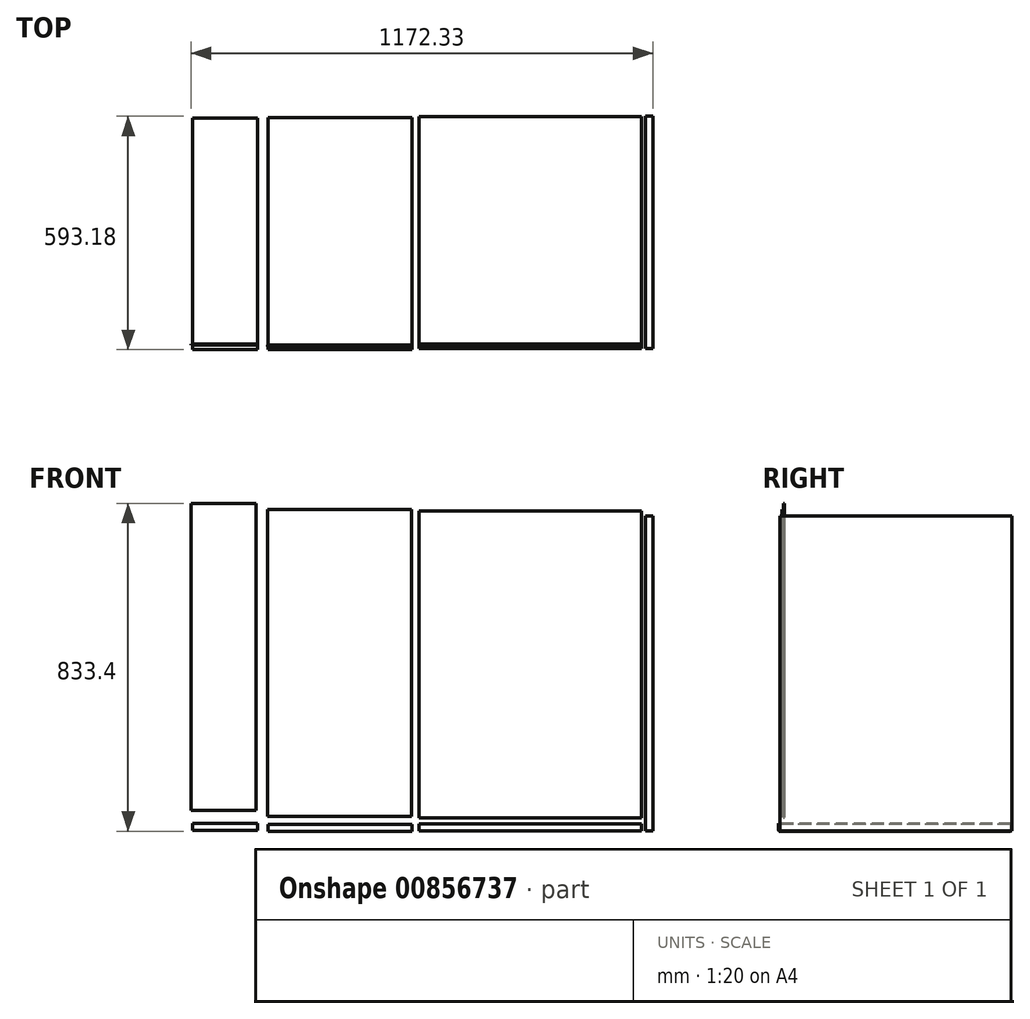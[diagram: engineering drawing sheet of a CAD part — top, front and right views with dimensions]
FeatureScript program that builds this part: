
annotation { "Feature Type Name" : "Feature", "Feature Type Description" : "" }
export const myFeature = defineFeature(function(context is Context, id is Id, definition is map)
    precondition{}
    {
        {
            var Q0;
            Q0=qCreatedBy(makeId("Top.planeOp"),FACE);
            var sketch = newSketch(context, id + "F0", { "sketchPlane" : qUnion([Q0])});
            skLineSegment(sketch, "E0.bottom", {"start": v(109.1, -315.54) * mm, "end": v(127.1, -315.54) * mm});
            skLineSegment(sketch, "E0.top", {"start": v(109.1, 274.46) * mm, "end": v(127.1, 274.46) * mm});
            skLineSegment(sketch, "E0.left", {"start": v(109.1, -315.54) * mm, "end": v(109.1, 274.46) * mm});
            skLineSegment(sketch, "E0.right", {"start": v(127.1, -315.54) * mm, "end": v(127.1, 274.46) * mm});
            skSolve(sketch);
        }
        {
            var Q0;
            Q0 = qSketchRegion(id + "F0", true);
            extrude(context, id + "F1", {"entities" : qUnion([Q0]), "depth" : 800 * mm, "offsetDistance" : 25 * mm});
        }
        {
            var Q0;
            Q0=qCreatedBy(makeId("Front.planeOp"),FACE);
            var sketch = newSketch(context, id + "F2", { "sketchPlane" : qUnion([Q0])});
            skLineSegment(sketch, "E1.bottom", {"start": v(-565, 364.26) * mm, "end": v(0, 364.26) * mm});
            skLineSegment(sketch, "E1.top", {"start": v(-565, -415.74) * mm, "end": v(0, -415.74) * mm});
            skLineSegment(sketch, "E1.left", {"start": v(-565, 364.26) * mm, "end": v(-565, -415.74) * mm});
            skLineSegment(sketch, "E1.right", {"start": v(0, 364.26) * mm, "end": v(0, -415.74) * mm});
            skSolve(sketch);
        }
        {
            var Q0;
            Q0 = qSketchRegion(id + "F2", true);
            extrude(context, id + "F3", {"entities" : qUnion([Q0]), "depth" : 3 * mm, "offsetDistance" : 25 * mm});
        }
        {
            var Q0;
            Q0=qCreatedBy(makeId("Top.planeOp"),FACE);
            var sketch = newSketch(context, id + "F4", { "sketchPlane" : qUnion([Q0])});
            skLineSegment(sketch, "E2.bottom", {"start": v(-523.86, -157.25) * mm, "end": v(41.14, -157.25) * mm});
            skLineSegment(sketch, "E2.top", {"start": v(-523.86, 431.75) * mm, "end": v(41.14, 431.75) * mm});
            skLineSegment(sketch, "E2.left", {"start": v(-523.86, -157.25) * mm, "end": v(-523.86, 431.75) * mm});
            skLineSegment(sketch, "E2.right", {"start": v(41.14, -157.25) * mm, "end": v(41.14, 431.75) * mm});
            skSolve(sketch);
        }
        {
            var Q0;
            Q0=makeQuery(id+"F4.imprint","IMPRINT",FACE,{"disambiguationData":[TD([[makeQuery(id+"F4.imprint","IMPRINT",EDGE,{"derivedFrom":sQuery(id+"F4.wireOp",EDGE,"E2.bottom")}),1.0]])]});
            extrude(context, id + "F5", {"entities" : qUnion([Q0]), "depth" : 18 * mm, "offsetDistance" : 25 * mm});
        }
        {
            var Q0;
            Q0=makeQuery(id+"F5.opExtrude","SWEPT_BODY",BODY,{"disambiguationData":[OSD([sQuery(id+"F4.wireOp",EDGE,"E2.bottom"),sQuery(id+"F4.wireOp",EDGE,"E2.top"),sQuery(id+"F4.wireOp",EDGE,"E2.left"),sQuery(id+"F4.wireOp",EDGE,"E2.right")])]});
            transform(context, id + "F6", {"entities" : qUnion([Q0]), "transformType" : TransformType.TRANSLATION_3D, "dx" : -113 * mm, "dy" : -67 * mm, "dz" : -330 * mm, "makeCopy" : false});
        }
        {
            var Q0;
            Q0=makeQuery(id+"F5.opExtrude","SWEPT_BODY",BODY,{"disambiguationData":[OSD([sQuery(id+"F4.wireOp",EDGE,"E2.bottom"),sQuery(id+"F4.wireOp",EDGE,"E2.top"),sQuery(id+"F4.wireOp",EDGE,"E2.left"),sQuery(id+"F4.wireOp",EDGE,"E2.right")])]});
            transform(context, id + "F7", {"entities" : qUnion([Q0]), "transformType" : TransformType.TRANSLATION_3D, "dx" : -127 * mm, "dy" : 213 * mm, "dz" : -119 * mm, "makeCopy" : false});
        }
        {
            var Q0;
            Q0=makeQuery(id+"F1.opExtrude","SWEPT_BODY",BODY,{"disambiguationData":[OSD([sQuery(id+"F0.wireOp",EDGE,"E0.bottom"),sQuery(id+"F0.wireOp",EDGE,"E0.top"),sQuery(id+"F0.wireOp",EDGE,"E0.left"),sQuery(id+"F0.wireOp",EDGE,"E0.right")])]});
            transform(context, id + "F8", {"entities" : qUnion([Q0]), "transformType" : TransformType.TRANSLATION_3D, "dx" : -98 * mm, "dy" : 304 * mm, "dz" : -449 * mm, "makeCopy" : false});
        }
        {
            var Q0;
            Q0=makeQuery(id+"F5.opExtrude","SWEPT_BODY",BODY,{"disambiguationData":[OSD([sQuery(id+"F4.wireOp",EDGE,"E2.bottom"),sQuery(id+"F4.wireOp",EDGE,"E2.top"),sQuery(id+"F4.wireOp",EDGE,"E2.left"),sQuery(id+"F4.wireOp",EDGE,"E2.right")])]});
            transform(context, id + "F9", {"entities" : qUnion([Q0]), "transformType" : TransformType.TRANSLATION_3D, "dx" : 0 * mm, "dy" : 0 * mm, "dz" : -52 * mm, "makeCopy" : true});
        }
        {
            var Q0;
            Q0=makeQuery(id+"F9.opPattern","COPY",BODY,{"derivedFrom":makeQuery(id+"F5.opExtrude","SWEPT_BODY",BODY,{"disambiguationData":[OSD([sQuery(id+"F4.wireOp",EDGE,"E2.bottom"),sQuery(id+"F4.wireOp",EDGE,"E2.top"),sQuery(id+"F4.wireOp",EDGE,"E2.left"),sQuery(id+"F4.wireOp",EDGE,"E2.right")])]}),"instanceName":"1"});
            deleteBodies(context, id + "F10", {"entities" : qUnion([Q0])});
        }
        {
            var Q0;
            Q0=makeQuery(id+"F4.imprint","IMPRINT",FACE,{"disambiguationData":[TD([[makeQuery(id+"F4.imprint","IMPRINT",EDGE,{"derivedFrom":sQuery(id+"F4.wireOp",EDGE,"E2.bottom")}),1.0]])]});
            var sketch = newSketch(context, id + "F11", { "sketchPlane" : qUnion([Q0])});
            skLineSegment(sketch, "E3.bottom", {"start": v(-1010.8, 367.55) * mm, "end": v(-645.8, 367.55) * mm});
            skLineSegment(sketch, "E3.top", {"start": v(-1010.8, -221.45) * mm, "end": v(-645.8, -221.45) * mm});
            skLineSegment(sketch, "E3.left", {"start": v(-1010.8, 367.55) * mm, "end": v(-1010.8, -221.45) * mm});
            skLineSegment(sketch, "E3.right", {"start": v(-645.8, 367.55) * mm, "end": v(-645.8, -221.45) * mm});
            skSolve(sketch);
        }
        {
            var Q0;
            Q0=makeQuery(id+"F5.opExtrude","SWEPT_BODY",BODY,{"disambiguationData":[OSD([sQuery(id+"F4.wireOp",EDGE,"E2.bottom"),sQuery(id+"F4.wireOp",EDGE,"E2.top"),sQuery(id+"F4.wireOp",EDGE,"E2.left"),sQuery(id+"F4.wireOp",EDGE,"E2.right")])]});
            transform(context, id + "F12", {"entities" : qUnion([Q0]), "transformType" : TransformType.TRANSLATION_3D, "dx" : 199 * mm, "dy" : 0 * mm, "dz" : 0 * mm, "makeCopy" : false});
        }
        {
            var Q0;
            Q0=makeQuery(id+"F11.imprint","IMPRINT",FACE,{"disambiguationData":[TD([[makeQuery(id+"F11.imprint","IMPRINT",EDGE,{"derivedFrom":sQuery(id+"F11.wireOp",EDGE,"E3.bottom")}),-1.0]])]});
            extrude(context, id + "F13", {"entities" : qUnion([Q0]), "depth" : 18 * mm, "offsetDistance" : 25 * mm});
        }
        {
            var Q0;
            Q0=makeQuery(id+"F13.opExtrude","SWEPT_BODY",BODY,{"disambiguationData":[OSD([sQuery(id+"F11.wireOp",EDGE,"E3.bottom"),sQuery(id+"F11.wireOp",EDGE,"E3.top"),sQuery(id+"F11.wireOp",EDGE,"E3.left"),sQuery(id+"F11.wireOp",EDGE,"E3.right")])]});
            transform(context, id + "F14", {"entities" : qUnion([Q0]), "transformType" : TransformType.TRANSLATION_3D, "dx" : 63 * mm, "dy" : 207 * mm, "dz" : -450 * mm, "makeCopy" : false});
        }
        {
            var Q0;
            Q0=makeQuery(id+"F3.opExtrude","CAP_FACE",FACE,{"disambiguationData":[OSD([sQuery(id+"F2.wireOp",EDGE,"E1.bottom"),sQuery(id+"F2.wireOp",EDGE,"E1.top"),sQuery(id+"F2.wireOp",EDGE,"E1.left"),sQuery(id+"F2.wireOp",EDGE,"E1.right")])],"isStart":false});
            var sketch = newSketch(context, id + "F15", { "sketchPlane" : qUnion([Q0])});
            skLineSegment(sketch, "E4.bottom", {"start": v(-1125.1, 719.67) * mm, "end": v(-760.1, 719.67) * mm});
            skLineSegment(sketch, "E4.top", {"start": v(-1125.1, -60.33) * mm, "end": v(-760.1, -60.33) * mm});
            skLineSegment(sketch, "E4.left", {"start": v(-1125.1, 719.67) * mm, "end": v(-1125.1, -60.33) * mm});
            skLineSegment(sketch, "E4.right", {"start": v(-760.1, 719.67) * mm, "end": v(-760.1, -60.33) * mm});
            skSolve(sketch);
        }
        {
            var Q0;
            Q0=makeQuery(id+"F15.imprint","IMPRINT",FACE,{"disambiguationData":[TD([[makeQuery(id+"F15.imprint","IMPRINT",EDGE,{"derivedFrom":sQuery(id+"F15.wireOp",EDGE,"E4.bottom")}),-1.0]])]});
            extrude(context, id + "F16", {"entities" : qUnion([Q0]), "depth" : 3 * mm, "offsetDistance" : 25 * mm});
        }
        {
            var Q0;
            Q0=makeQuery(id+"F16.opExtrude","SWEPT_BODY",BODY,{"disambiguationData":[OSD([sQuery(id+"F15.wireOp",EDGE,"E4.bottom"),sQuery(id+"F15.wireOp",EDGE,"E4.top"),sQuery(id+"F15.wireOp",EDGE,"E4.left"),sQuery(id+"F15.wireOp",EDGE,"E4.right")])]});
            transform(context, id + "F17", {"entities" : qUnion([Q0]), "transformType" : TransformType.TRANSLATION_3D, "dx" : 176 * mm, "dy" : 0 * mm, "dz" : -352 * mm, "makeCopy" : false});
        }
        {
            var Q0;
            Q0=qCreatedBy(makeId("Top.planeOp"),FACE);
            var sketch = newSketch(context, id + "F18", { "sketchPlane" : qUnion([Q0])});
            skLineSegment(sketch, "E5.bottom", {"start": v(-1134.45, 564.28) * mm, "end": v(-969.45, 564.28) * mm});
            skLineSegment(sketch, "E5.top", {"start": v(-1134.45, -24.72) * mm, "end": v(-969.45, -24.72) * mm});
            skLineSegment(sketch, "E5.left", {"start": v(-1134.45, 564.28) * mm, "end": v(-1134.45, -24.72) * mm});
            skLineSegment(sketch, "E5.right", {"start": v(-969.45, 564.28) * mm, "end": v(-969.45, -24.72) * mm});
            skSolve(sketch);
        }
        {
            var Q0;
            Q0=makeQuery(id+"F18.imprint","IMPRINT",FACE,{"disambiguationData":[TD([[makeQuery(id+"F18.imprint","IMPRINT",EDGE,{"derivedFrom":sQuery(id+"F18.wireOp",EDGE,"E5.bottom")}),-1.0]])]});
            extrude(context, id + "F19", {"entities" : qUnion([Q0]), "depth" : 18 * mm, "offsetDistance" : 25 * mm});
        }
        {
            var Q0;
            Q0=makeQuery(id+"F19.opExtrude","SWEPT_BODY",BODY,{"disambiguationData":[OSD([sQuery(id+"F18.wireOp",EDGE,"E5.bottom"),sQuery(id+"F18.wireOp",EDGE,"E5.top"),sQuery(id+"F18.wireOp",EDGE,"E5.left"),sQuery(id+"F18.wireOp",EDGE,"E5.right")])]});
            transform(context, id + "F20", {"entities" : qUnion([Q0]), "transformType" : TransformType.TRANSLATION_3D, "dx" : -5 * mm, "dy" : 10 * mm, "dz" : 0 * mm, "makeCopy" : false});
        }
        {
            var Q0;
            Q0=makeQuery(id+"F19.opExtrude","SWEPT_BODY",BODY,{"disambiguationData":[OSD([sQuery(id+"F18.wireOp",EDGE,"E5.bottom"),sQuery(id+"F18.wireOp",EDGE,"E5.top"),sQuery(id+"F18.wireOp",EDGE,"E5.left"),sQuery(id+"F18.wireOp",EDGE,"E5.right")])]});
            transform(context, id + "F21", {"entities" : qUnion([Q0]), "transformType" : TransformType.TRANSLATION_3D, "dx" : 0 * mm, "dy" : 0 * mm, "dz" : -448 * mm, "makeCopy" : false});
        }
        {
            var Q0;
            Q0=qCreatedBy(makeId("Front.planeOp"),FACE);
            var sketch = newSketch(context, id + "F22", { "sketchPlane" : qUnion([Q0])});
            skLineSegment(sketch, "E6.bottom", {"start": v(-1143.23, 383.4) * mm, "end": v(-978.23, 383.4) * mm});
            skLineSegment(sketch, "E6.top", {"start": v(-1143.23, -396.6) * mm, "end": v(-978.23, -396.6) * mm});
            skLineSegment(sketch, "E6.left", {"start": v(-1143.23, 383.4) * mm, "end": v(-1143.23, -396.6) * mm});
            skLineSegment(sketch, "E6.right", {"start": v(-978.23, 383.4) * mm, "end": v(-978.23, -396.6) * mm});
            skSolve(sketch);
        }
        {
            var Q0;
            Q0 = qSketchRegion(id + "F22", true);
            extrude(context, id + "F23", {"entities" : qUnion([Q0]), "depth" : 3 * mm, "offsetDistance" : 25 * mm});
        }
    });
